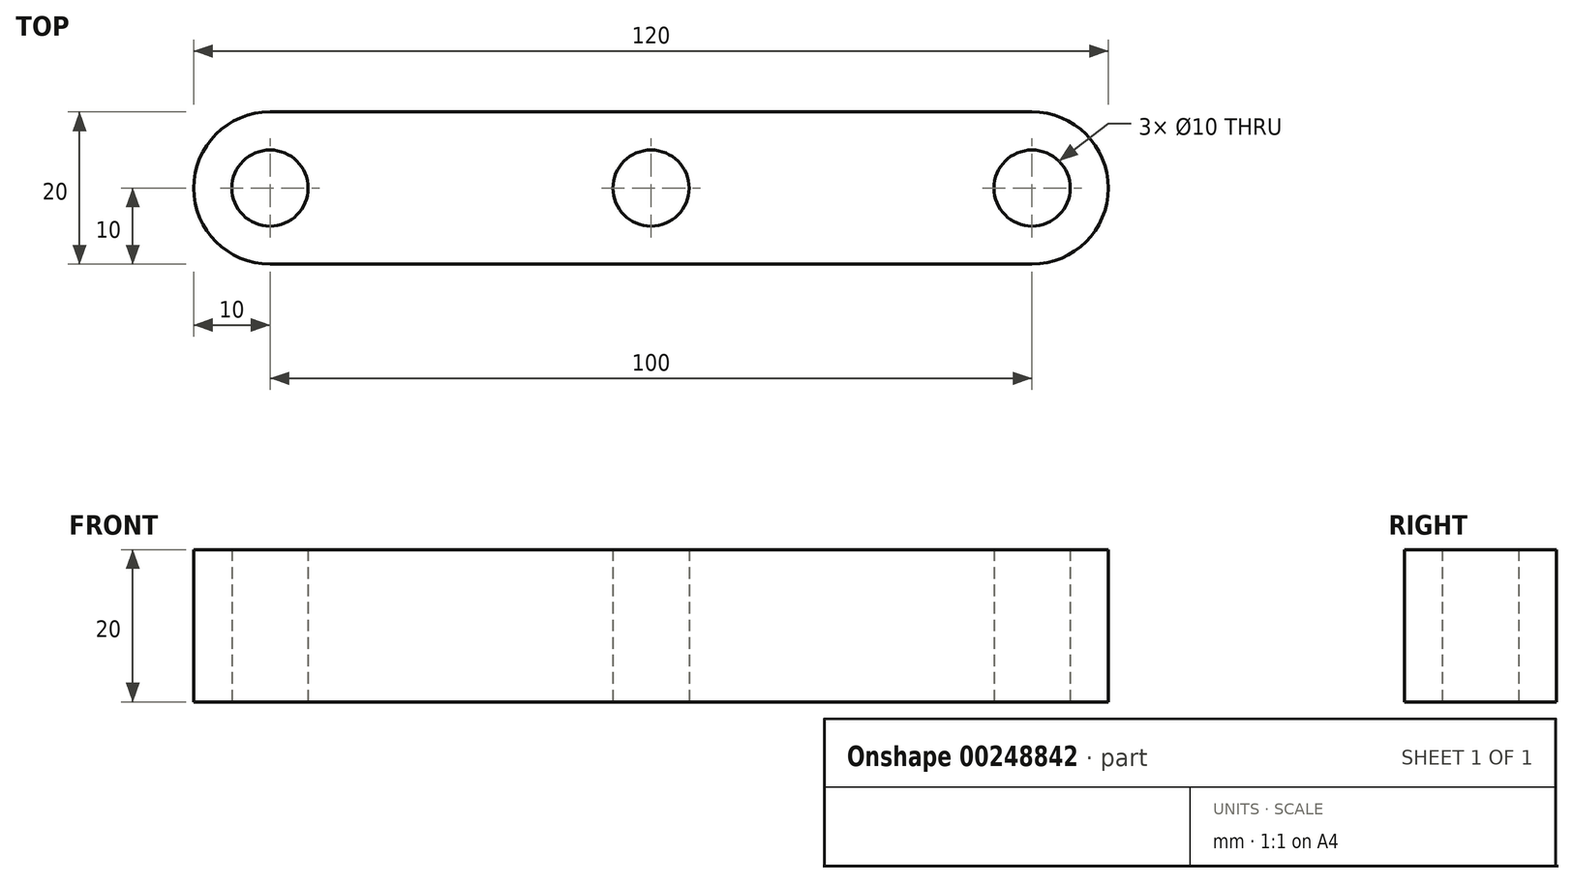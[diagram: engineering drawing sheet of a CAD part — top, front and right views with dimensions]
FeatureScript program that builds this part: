
annotation { "Feature Type Name" : "Feature", "Feature Type Description" : "" }
export const myFeature = defineFeature(function(context is Context, id is Id, definition is map)
    precondition{}
    {
        {
            var Q0;
            Q0=qCreatedBy(makeId("Top.planeOp"),FACE);
            var sketch = newSketch(context, id + "F0", { "sketchPlane" : qUnion([Q0])});
            skLineSegment(sketch, "E0.bottom", {"start": v(-50, 10) * mm, "end": v(50, 10) * mm});
            skLineSegment(sketch, "E0.top", {"start": v(-50, -10) * mm, "end": v(50, -10) * mm});
            skPoint(sketch, "E0.middle", {"position": v(0, 0) * mm});
            skCircle(sketch, "E1", {"center": v(0, 0) * mm, "radius": 5 * mm});
            skCircle(sketch, "E2", {"center": v(50, 0) * mm, "radius": 5 * mm});
            skCircle(sketch, "E3", {"center": v(-50, 0) * mm, "radius": 5 * mm});
            skArc(sketch, "E4", {"start": v(-50, 10) * mm, "mid": v(-60, 0) * mm, "end": v(-50, -10) * mm});
            skArc(sketch, "E5", {"start": v(50, 10) * mm, "mid": v(60, 0) * mm, "end": v(50, -10) * mm});
            skSolve(sketch);
        }
        {
            var Q0;
            Q0=makeQuery(id+"F0.imprint","IMPRINT",FACE,{"disambiguationData":[TD([[makeQuery(id+"F0.imprint","IMPRINT",EDGE,{"derivedFrom":sQuery(id+"F0.wireOp",EDGE,"E0.bottom")}),-1.0]])]});
            extrude(context, id + "F1", {"entities" : qUnion([Q0]), "endBound" : BoundingType.SYMMETRIC, "depth" : 20 * mm});
        }
    });
